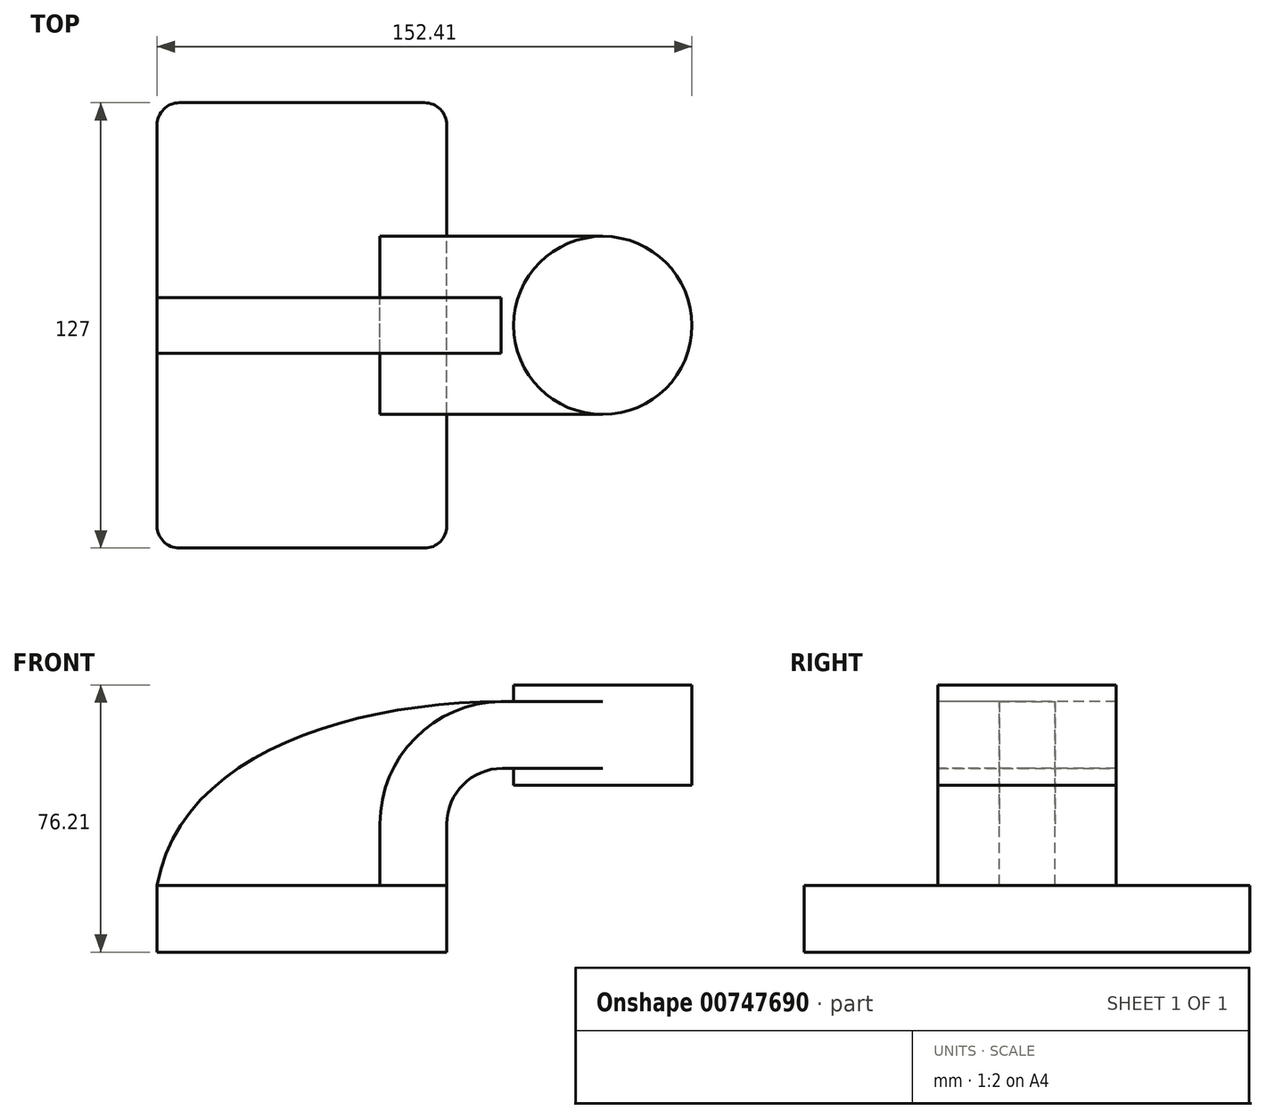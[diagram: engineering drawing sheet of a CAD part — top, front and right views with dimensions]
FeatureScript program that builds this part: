
annotation { "Feature Type Name" : "Feature", "Feature Type Description" : "" }
export const myFeature = defineFeature(function(context is Context, id is Id, definition is map)
    precondition{}
    {
        {
            var Q0;
            Q0=qCreatedBy(makeId("Front.planeOp"),FACE);
            var sketch = newSketch(context, id + "F0", { "sketchPlane" : qUnion([Q0])});
            skLineSegment(sketch, "E0.bottom", {"start": v(41.28, -9.52) * mm, "end": v(-41.27, -9.53) * mm});
            skLineSegment(sketch, "E0.top", {"start": v(41.28, 9.53) * mm, "end": v(-41.28, 9.53) * mm});
            skLineSegment(sketch, "E0.left", {"start": v(41.28, -9.52) * mm, "end": v(41.28, 9.53) * mm});
            skLineSegment(sketch, "E0.right", {"start": v(-41.28, -9.53) * mm, "end": v(-41.28, 9.52) * mm});
            skPoint(sketch, "E0.middle", {"position": v(0, 0) * mm});
            skLineSegment(sketch, "E1.bottom", {"start": v(111.13, 38.1) * mm, "end": v(60.33, 38.1) * mm});
            skLineSegment(sketch, "E1.top", {"start": v(111.13, 66.68) * mm, "end": v(60.33, 66.68) * mm});
            skLineSegment(sketch, "E1.left", {"start": v(111.13, 38.1) * mm, "end": v(111.13, 66.68) * mm});
            skLineSegment(sketch, "E1.right", {"start": v(60.33, 38.1) * mm, "end": v(60.33, 66.68) * mm});
            skPoint(sketch, "E1.middle", {"position": v(85.73, 52.39) * mm});
            skLineSegment(sketch, "E2", {"start": v(41.28, 9.53) * mm, "end": v(41.28, 27) * mm});
            skArc(sketch, "E3", {"start": v(41.27, 27) * mm, "mid": v(45.92, 38.23) * mm, "end": v(57.15, 42.88) * mm});
            skLineSegment(sketch, "E4", {"start": v(57.15, 42.88) * mm, "end": v(85.72, 42.88) * mm});
            skLineSegment(sketch, "E5.0", {"start": v(57.15, 61.93) * mm, "end": v(85.72, 61.93) * mm});
            skArc(sketch, "E5.1", {"start": v(22.23, 27) * mm, "mid": v(32.45, 51.7) * mm, "end": v(57.15, 61.93) * mm});
            skLineSegment(sketch, "E5.2", {"start": v(22.22, 9.53) * mm, "end": v(22.22, 27) * mm});
            skLineSegment(sketch, "E6", {"start": v(85.73, 38.1) * mm, "end": v(85.73, 66.68) * mm});
            skFitSpline(sketch, "E7", {"points": [v(-41.28, 9.52) * mm, v(57.15, 61.93) * mm], "startDerivative": vector(19.03, 109) * mm, "endDerivative": vector(137.39, 0.72) * mm});
            skSolve(sketch);
        }
        {
            var Q0;
            Q0=makeQuery(id+"F0.imprint","IMPRINT",FACE,{"disambiguationData":[TD([[makeQuery(id+"F0.imprint","IMPRINT",EDGE,{"derivedFrom":sQuery(id+"F0.wireOp",EDGE,"E0.bottom")}),-1.0]])]});
            extrude(context, id + "F1", {"entities" : qUnion([Q0]), "endBound" : BoundingType.SYMMETRIC, "depth" : 127 * mm, "offsetDistance" : 25.4 * mm});
        }
        {
            var Q0;
            {var subQ1=sQuery(id+"F0.wireOp",EDGE,"E2");Q0=makeQuery(id+"F0.imprint","IMPRINT",FACE,{"disambiguationData":[TD([[makeQuery(id+"F0.imprint","IMPRINT",EDGE,{"derivedFrom":subQ1}),1.0]])]});}
            var Q1;
            {var subQ0=sQuery(id+"F0.wireOp",EDGE,"E4");var subQ1=sQuery(id+"F0.wireOp",EDGE,"E1.right");var subQ2=makeQuery(id+"F0.imprint","INTERSECT",VERTEX,{"derivedFrom":[subQ1,subQ0]});Q1=makeQuery(id+"F0.imprint","IMPRINT",FACE,{"disambiguationData":[TD([[makeQuery(id+"F0.imprint","IMPRINT",EDGE,{"disambiguationData":[TD([[subQ2,-1.0]])],"derivedFrom":subQ1}),-1.0]])]});}
            extrude(context, id + "F2", {"entities" : qUnion([Q0, Q1]), "endBound" : BoundingType.SYMMETRIC, "depth" : 50.8 * mm, "offsetDistance" : 25.4 * mm});
        }
        {
            var Q0;
            {var subQ3=sQuery(id+"F0.wireOp",EDGE,"E5.2");Q0=makeQuery(id+"F0.imprint","IMPRINT",FACE,{"disambiguationData":[TD([[makeQuery(id+"F0.imprint","IMPRINT",EDGE,{"derivedFrom":subQ3}),1.0]])]});}
            extrude(context, id + "F3", {"entities" : qUnion([Q0]), "endBound" : BoundingType.SYMMETRIC, "depth" : 15.85 * mm, "offsetDistance" : 25.4 * mm});
        }
        {
            var Q0;
            {var subQ0=sQuery(id+"F0.wireOp",EDGE,"E1.left");Q0=makeQuery(id+"F0.imprint","IMPRINT",FACE,{"disambiguationData":[TD([[makeQuery(id+"F0.imprint","IMPRINT",EDGE,{"derivedFrom":subQ0}),1.0]])]});}
            var Q1;
            Q1=sQuery(id+"F0.wireOp",EDGE,"E6");
            revolve(context, id + "F4", {"operationType" : NewBodyOperationType.ADD, "surfaceOperationType" : NewSurfaceOperationType.NEW, "entities" : qUnion([Q0]), "axis" : qUnion([Q1]), "revolveType" : RevolveType.FULL});
        }
        {
            var Q0;
            Q0=makeQuery(id+"F1.opExtrude","CAP_EDGE",EDGE,{"disambiguationData":[OSD([sQuery(id+"F0.wireOp",EDGE,"E0.right")])],"isStart":false});
            var Q1;
            Q1=makeQuery(id+"F1.opExtrude","CAP_EDGE",EDGE,{"disambiguationData":[OSD([sQuery(id+"F0.wireOp",EDGE,"E0.left")])],"isStart":false});
            var Q2;
            Q2=makeQuery(id+"F1.opExtrude","CAP_EDGE",EDGE,{"disambiguationData":[OSD([sQuery(id+"F0.wireOp",EDGE,"E0.left")])],"isStart":true});
            var Q3;
            Q3=makeQuery(id+"F1.opExtrude","CAP_EDGE",EDGE,{"disambiguationData":[OSD([sQuery(id+"F0.wireOp",EDGE,"E0.right")])],"isStart":true});
            fillet(context, id + "F5", {"entities" : qUnion([Q0, Q1, Q2, Q3]), "radius" : 6.35 * mm, "tangentPropagation" : true, "allowEdgeOverflow" : false});
        }
    });
